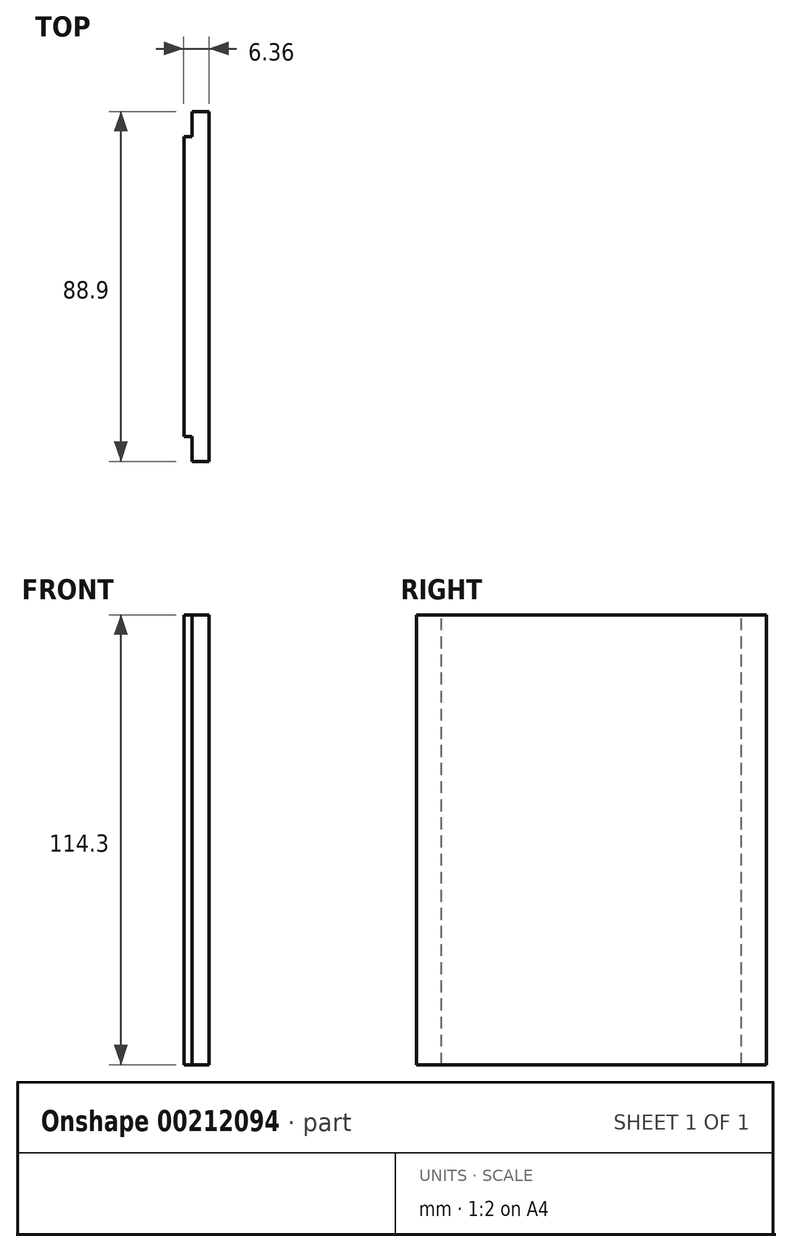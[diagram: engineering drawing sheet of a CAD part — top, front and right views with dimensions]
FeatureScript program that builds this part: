
annotation { "Feature Type Name" : "Feature", "Feature Type Description" : "" }
export const myFeature = defineFeature(function(context is Context, id is Id, definition is map)
    precondition{}
    {
        {
            var Q0;
            Q0=qCreatedBy(makeId("Right.planeOp"),FACE);
            var sketch = newSketch(context, id + "F0", { "sketchPlane" : qUnion([Q0])});
            skLineSegment(sketch, "E0.bottom", {"start": v(0, 0) * mm, "end": v(88.9, 0) * mm});
            skLineSegment(sketch, "E0.top", {"start": v(0, 114.3) * mm, "end": v(88.9, 114.3) * mm});
            skLineSegment(sketch, "E0.left", {"start": v(0, 0) * mm, "end": v(0, 114.3) * mm});
            skLineSegment(sketch, "E0.right", {"start": v(88.9, 0) * mm, "end": v(88.9, 114.3) * mm});
            skSolve(sketch);
        }
        {
            var Q0;
            Q0=makeQuery(id+"F0.imprint","IMPRINT",FACE,{"disambiguationData":[TD([[makeQuery(id+"F0.imprint","IMPRINT",EDGE,{"derivedFrom":sQuery(id+"F0.wireOp",EDGE,"E0.bottom")}),1.0]])]});
            var Q1;
            Q1 = qSketchRegion(id + "F2", true);
            extrude(context, id + "F1", {"entities" : qUnion([Q0, Q1]), "depth" : 4.24 * mm});
        }
        {
            var Q0;
            Q0=qCreatedBy(makeId("Right.planeOp"),FACE);
            var sketch = newSketch(context, id + "F2", { "sketchPlane" : qUnion([Q0])});
            skLineSegment(sketch, "E1.bottom", {"start": v(6.35, 0) * mm, "end": v(82.55, 0) * mm});
            skLineSegment(sketch, "E1.top", {"start": v(6.35, 114.3) * mm, "end": v(82.55, 114.3) * mm});
            skLineSegment(sketch, "E1.left", {"start": v(6.35, 0) * mm, "end": v(6.35, 114.3) * mm});
            skLineSegment(sketch, "E1.right", {"start": v(82.55, 0) * mm, "end": v(82.55, 114.3) * mm});
            skSolve(sketch);
        }
        {
            var Q0;
            Q0 = qSketchRegion(id + "F2", true);
            extrude(context, id + "F3", {"entities" : qUnion([Q0]), "operationType" : NewBodyOperationType.ADD, "oppositeDirection" : true, "depth" : 2.12 * mm});
        }
    });
